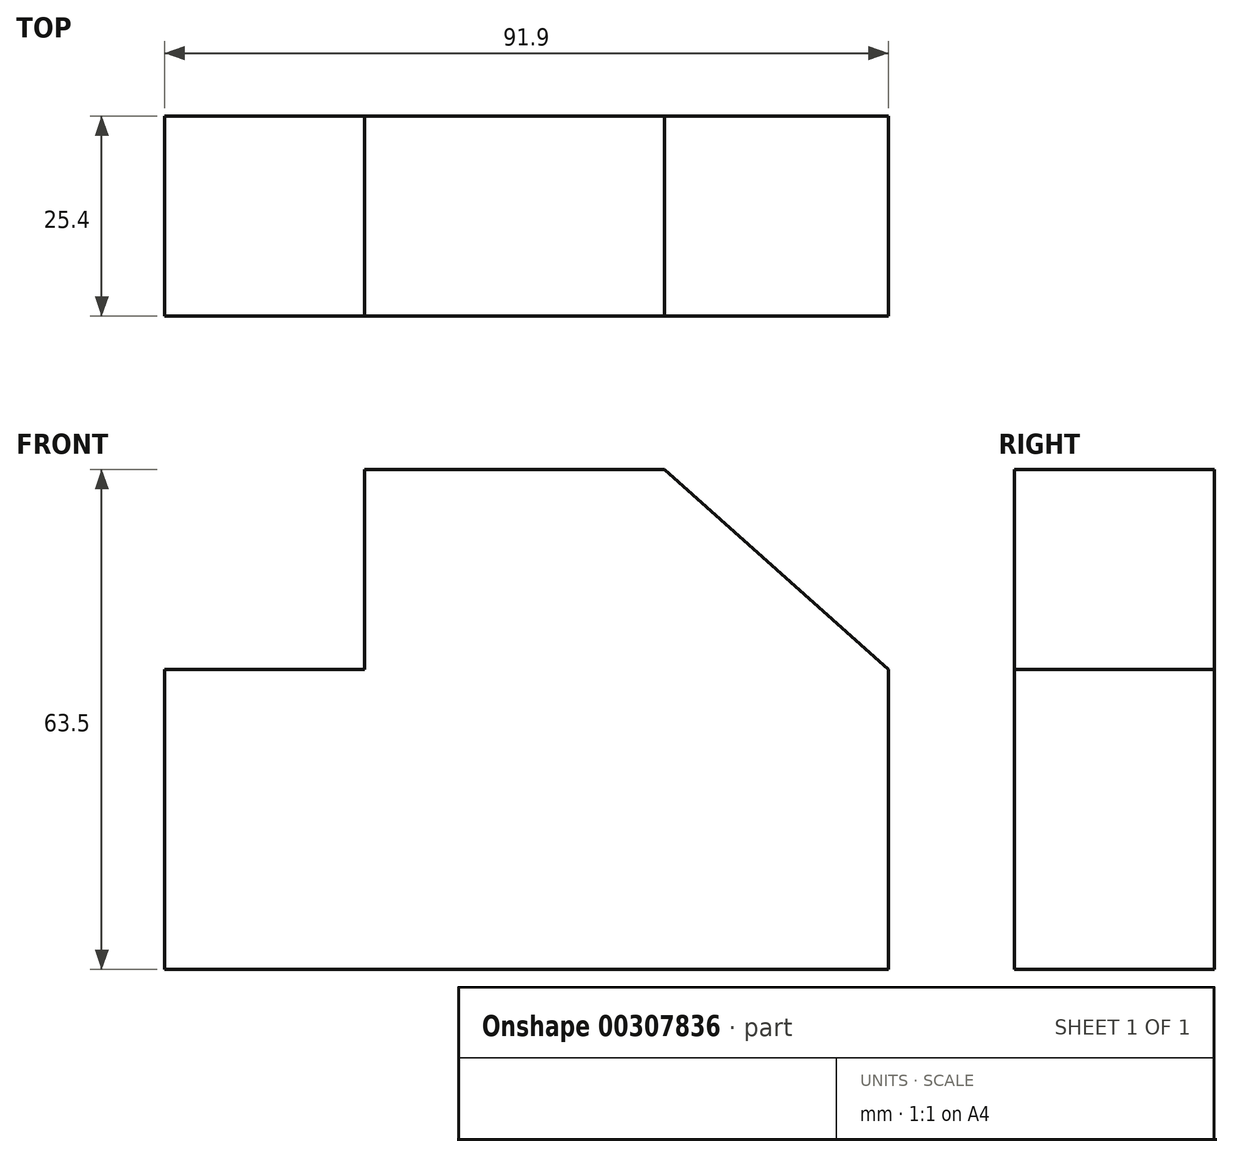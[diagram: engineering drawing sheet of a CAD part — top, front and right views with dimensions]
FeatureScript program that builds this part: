
annotation { "Feature Type Name" : "Feature", "Feature Type Description" : "" }
export const myFeature = defineFeature(function(context is Context, id is Id, definition is map)
    precondition{}
    {
        {
            var Q0;
            Q0=qCreatedBy(makeId("Front.planeOp"),FACE);
            var sketch = newSketch(context, id + "F0", { "sketchPlane" : qUnion([Q0])});
            skLineSegment(sketch, "E0", {"start": v(-36.66, -22.6) * mm, "end": v(55.24, -22.6) * mm});
            skLineSegment(sketch, "E1", {"start": v(-36.66, -22.6) * mm, "end": v(-36.66, 15.5) * mm});
            skLineSegment(sketch, "E2", {"start": v(55.24, -22.6) * mm, "end": v(55.24, 15.5) * mm});
            skLineSegment(sketch, "E3", {"start": v(-36.66, 15.5) * mm, "end": v(-11.26, 15.5) * mm});
            skLineSegment(sketch, "E4", {"start": v(-11.26, 15.5) * mm, "end": v(-11.26, 40.9) * mm});
            skLineSegment(sketch, "E5", {"start": v(-11.26, 40.9) * mm, "end": v(26.84, 40.9) * mm});
            skLineSegment(sketch, "E6", {"start": v(26.84, 40.9) * mm, "end": v(55.24, 15.5) * mm});
            skSolve(sketch);
        }
        {
            var Q0;
            Q0=makeQuery(id+"F0.imprint","IMPRINT",FACE,{"disambiguationData":[TD([[makeQuery(id+"F0.imprint","IMPRINT",EDGE,{"derivedFrom":sQuery(id+"F0.wireOp",EDGE,"E0")}),1.0]])]});
            extrude(context, id + "F1", {"entities" : qUnion([Q0]), "depth" : 25.4 * mm});
        }
    });
